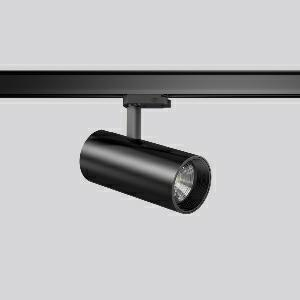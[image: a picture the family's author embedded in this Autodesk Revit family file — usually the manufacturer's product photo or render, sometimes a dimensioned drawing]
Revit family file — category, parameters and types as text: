
# Revit family: deecos_s_mini_742198_003_3_76_4423
name_source: partatom
category: Lighting Fixtures
units: mm (PartAtom-declared; Revit-internal decimal feet)

## family parameters
Cut with Voids When Loaded = No
Host = Face
Light Source = No
Part Type = Normal
Room Calculation Point = No
Round Connector Dimension = Use Diameter
Shared = No

## types (1)
- DEECOS S mini (1 x LED Modul 935, 2250 lm, 3500)
    Apparent Load = 20 VA
    Approval mark = CE
    CIE Flux Codes = 99 100 100 100 100
    Color Rendering = 92
    Color Temperature = 3500
    Default Elevation = 1800 mm
    Description = Series: DEECOS S mini
LED surface-mounted projector in modern design with no visible cooling ribs. Housing: die-cast aluminium, powder-coated. Rotation range: 356°. Swivel range: 90°. Black plastic ring and recessed LED to prevent glare from the side. Optical assembly with lens made of plastic (polycarbonate) for the best homogeneous light distribution - can be changed without tools. Best colour rendering index Ra>90. With adapter for RZB 3-circuit DALI tracks. Suitable for Track on ceiling, Wall track. High quality converter without flickering and stroboscopic effect. The following accessories can be mounted without use of tools: interchangeable lenses, decorative glasses, honeycomb louvre, clear and frosted diffusers, white interchangeable plastic ring. 
Colour: deep black, matt (RAL 9005)
Diameter: 87 mm
Height: 214 mm
Lamp: LED
Socket: without socket
Colour temperature: 3500K
Colour rendering index (CRI): 92
System power: 20 W
Rated luminous flux: 2250 lm
Luminous efficiency: 113 lm/W
Control gear: Converter, dimmable, DALI
Protection class: I
Type of protection: IP 20
    Height = 214 mm
    Lamp = 1 x LED Modul 935
    Lamp Light Flux = 2250 lm
    Lamp count = 1
    Length = 87 mm
    Lifetime = 50000 h
    Luminous efficacy = 113 lm/W
    Manufacturer = RZB
    ModVariant = No
    Model = 742198.003.3.76
    Mounting Place = Ceiling
    Mounting Type = Rail mounted
    Number of Poles = 1
    OnlyDefault = Yes
    Power Factor = 1
    Product Name = DEECOS S mini
    Product group = Track mounted projectors
    ProductGroupID = 301
    Protection Class = Protection class I
    Protection Degree = IP 20
    RLX_Detail_Level = 1
    RLX_Emergency_Light_Flux = 0 lm
    RLX_Emergency_Type = 0
    RLX_Emergency_Type_DB = No
    RlxData = <blob elided: 38633 chars, md5=e3d84283>
    Socket = socket
    Standby Power = 0 W
    System Light Flux = 2250 lm
    System Power = 20 W
    Type Comments = Product without accessories
    Type Image = 741930.003.jpg
    URL = http://relux.com
    VarID = ---
    Voltage = 230 V
    Voltage Range = 220-240 V
    Weight = 0.00 kg
    Width = 0 mm  [stored 0 ft]

note: [stored X ft] marks values corroborated as IEEE doubles in the binary element streams (Revit-internal decimal feet)

## geometry (parser evidence)
native form markers: Blend x4, Sweep x12
no freeform markers — native parametric forms only
